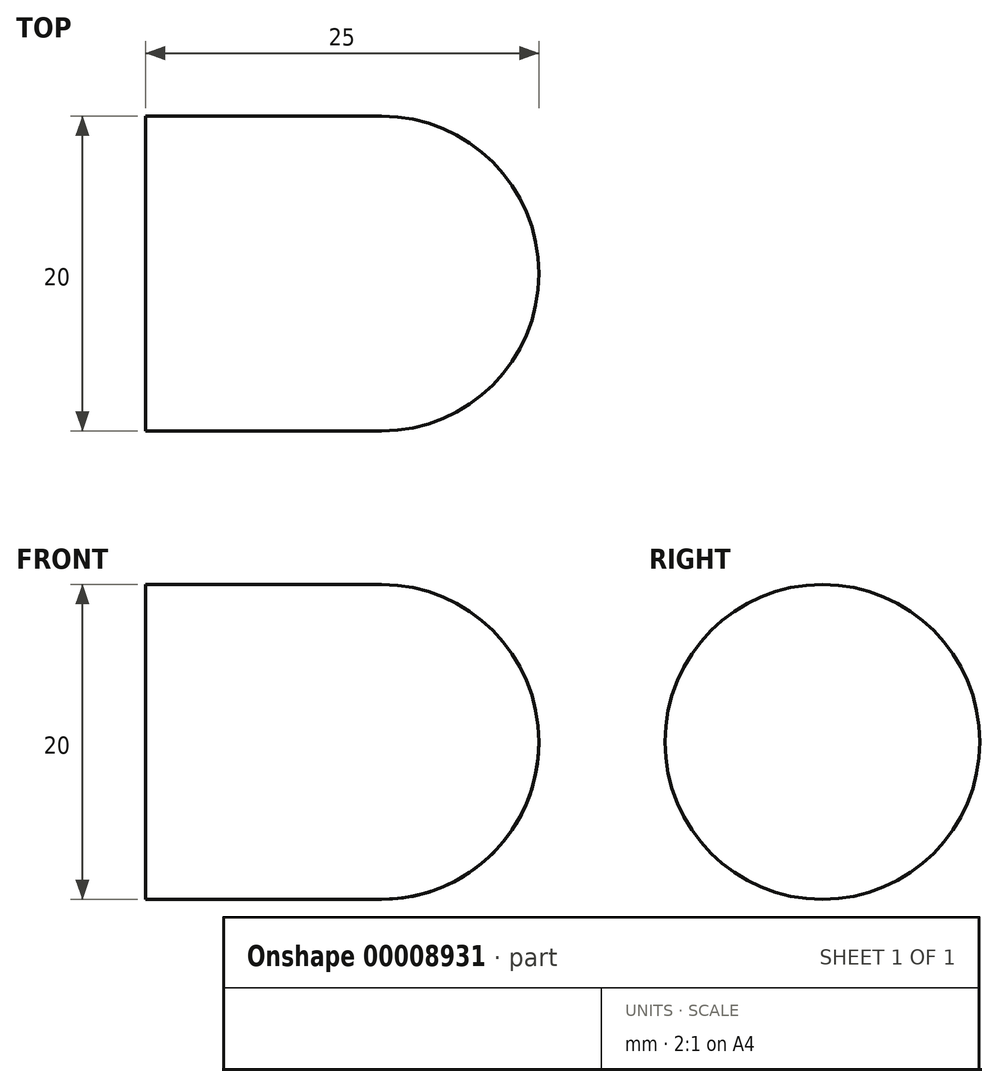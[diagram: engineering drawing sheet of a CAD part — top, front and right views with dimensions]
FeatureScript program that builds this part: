
annotation { "Feature Type Name" : "Feature", "Feature Type Description" : "" }
export const myFeature = defineFeature(function(context is Context, id is Id, definition is map)
    precondition{}
    {
        {
            var Q0;
            Q0=qCreatedBy(makeId("Right.planeOp"),FACE);
            var sketch = newSketch(context, id + "F0", { "sketchPlane" : qUnion([Q0])});
            skCircle(sketch, "E0", {"center": v(0, 0) * mm, "radius": 10 * mm});
            skLineSegment(sketch, "E1", {"start": v(0, 0) * mm, "end": v(10, 0) * mm});
            skSolve(sketch);
        }
        {
            var Q0;
            Q0=qSketchRegion(id+"F0",true);
            extrude(context, id + "F1", {"entities" : qUnion([Q0]), "depth" : 25 * mm});
        }
        {
            var Q0;
            Q0=makeQuery(id+"F1.opExtrude","CAP_FACE",FACE,{"disambiguationData":[OSD([sQuery(id+"F0.wireOp",EDGE,"E0")])],"isStart":false});
            fillet(context, id + "F2", {"entities" : qUnion([Q0]), "radius" : 10 * mm, "tangentPropagation" : true, "allowEdgeOverflow" : false});
        }
    });
